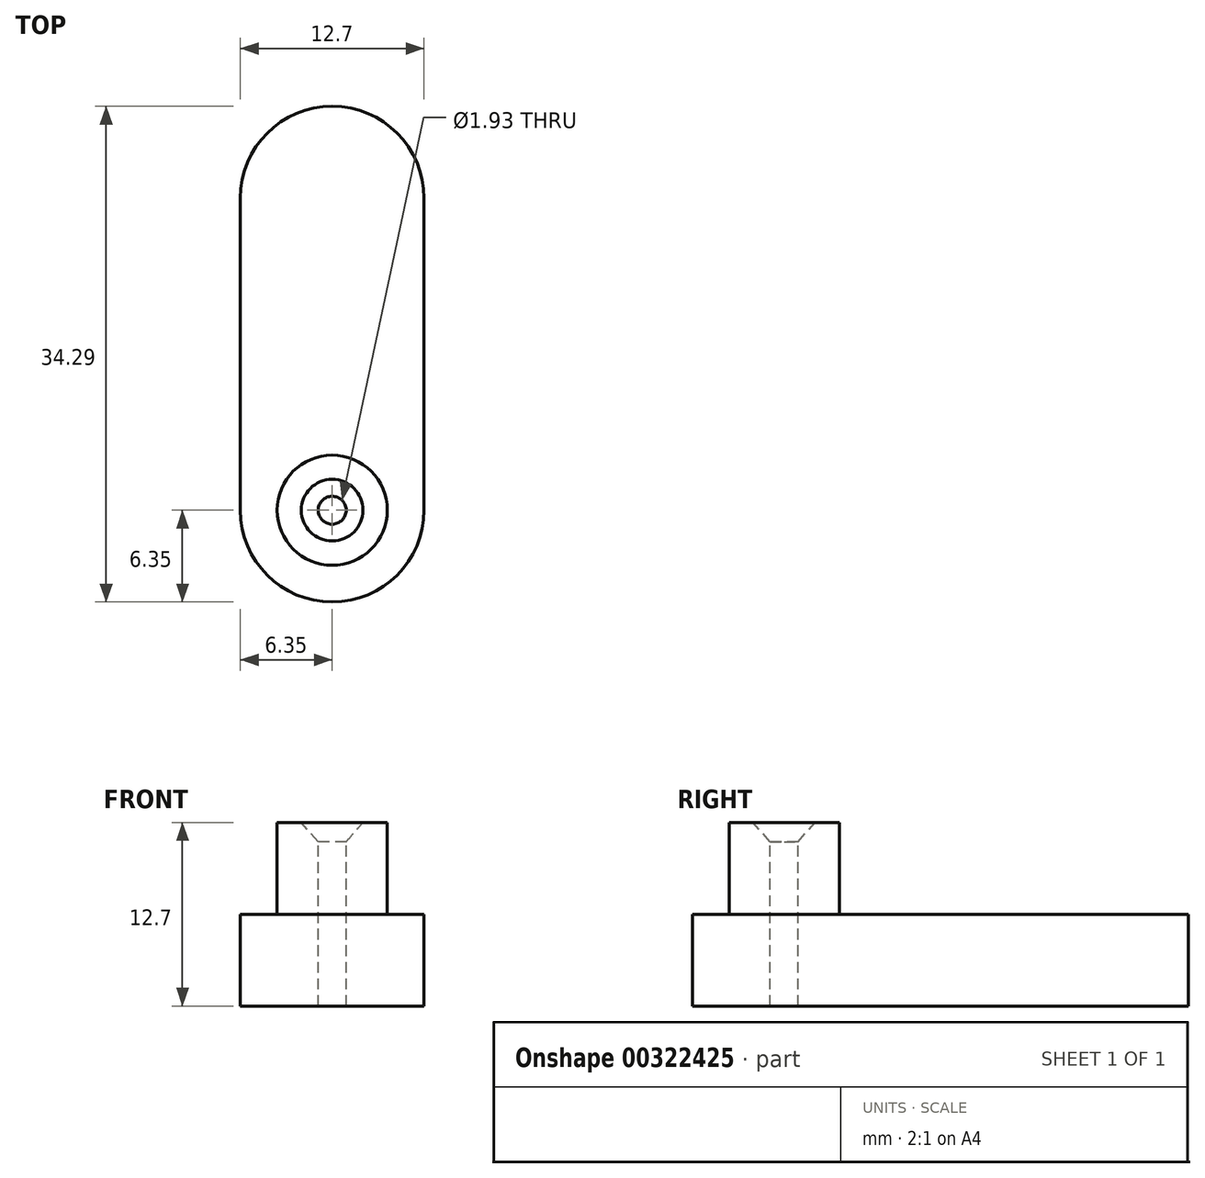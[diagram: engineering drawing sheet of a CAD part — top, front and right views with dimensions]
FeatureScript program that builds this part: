
annotation { "Feature Type Name" : "Feature", "Feature Type Description" : "" }
export const myFeature = defineFeature(function(context is Context, id is Id, definition is map)
    precondition{}
    {
        {
            var Q0;
            Q0=qCreatedBy(makeId("Top.planeOp"),FACE);
            var sketch = newSketch(context, id + "F0", { "sketchPlane" : qUnion([Q0])});
            skLineSegment(sketch, "E0", {"start": v(0, 12.7) * mm, "end": v(0, 34.3) * mm});
            skLineSegment(sketch, "E1", {"start": v(0, 34.3) * mm, "end": v(22.73, 67.98) * mm});
            skPoint(sketch, "E2", {"position": v(0, 0) * mm});
            skLineSegment(sketch, "E3", {"start": v(0, 12.7) * mm, "end": v(0, 0) * mm});
            skArc(sketch, "E4.0.startCap", {"start": v(6.35, 12.7) * mm, "mid": v(0, 6.35) * mm, "end": v(-6.35, 12.7) * mm});
            skArc(sketch, "E4.0.endCap", {"start": v(-6.35, 34.3) * mm, "mid": v(0, 40.64) * mm, "end": v(6.35, 34.3) * mm});
            skLineSegment(sketch, "E4.0.left", {"start": v(-6.35, 12.7) * mm, "end": v(-6.35, 34.3) * mm});
            skLineSegment(sketch, "E4.0.right", {"start": v(6.35, 12.7) * mm, "end": v(6.35, 34.3) * mm});
            skArc(sketch, "E4.1.startCap", {"start": v(-6.35, 12.7) * mm, "mid": v(0, 19.05) * mm, "end": v(6.35, 12.7) * mm});
            skArc(sketch, "E4.1.endCap", {"start": v(6.35, 0) * mm, "mid": v(0, -6.35) * mm, "end": v(-6.35, 0) * mm});
            skLineSegment(sketch, "E4.1.left", {"start": v(6.35, 12.7) * mm, "end": v(6.35, 0) * mm});
            skLineSegment(sketch, "E4.1.right", {"start": v(-6.35, 12.7) * mm, "end": v(-6.35, 0) * mm});
            skArc(sketch, "E4.2.startCap", {"start": v(5.26, 30.74) * mm, "mid": v(-3.55, 29.03) * mm, "end": v(-5.26, 37.84) * mm});
            skArc(sketch, "E4.2.endCap", {"start": v(17.46, 71.53) * mm, "mid": v(26.28, 73.25) * mm, "end": v(27.99, 64.43) * mm});
            skLineSegment(sketch, "E4.2.left", {"start": v(-5.26, 37.84) * mm, "end": v(17.46, 71.53) * mm});
            skLineSegment(sketch, "E4.2.right", {"start": v(5.26, 30.74) * mm, "end": v(27.99, 64.43) * mm});
            skSolve(sketch);
        }
        {
            var Q0;
            Q0=makeQuery(id+"F0.imprint","IMPRINT",FACE,{"disambiguationData":[TD([[makeQuery(id+"F0.imprint","IMPRINT",EDGE,{"derivedFrom":sQuery(id+"F0.wireOp",EDGE,"E4.1.endCap")}),-1.0]])]});
            var Q1;
            {var subQ0=sQuery(id+"F0.wireOp",EDGE,"E3");var subQ1=sQuery(id+"F0.wireOp",EDGE,"E0");var subQ2=makeQuery(id+"F0.imprint","INTERSECT",VERTEX,{"derivedFrom":[subQ1,subQ0]});Q1=makeQuery(id+"F0.imprint","IMPRINT",FACE,{"disambiguationData":[TD([[makeQuery(id+"F0.imprint","IMPRINT",EDGE,{"disambiguationData":[TD([[subQ2,-1.0]])],"derivedFrom":subQ1}),1.0]])]});}
            var Q2;
            {var subQ0=sQuery(id+"F0.wireOp",EDGE,"E3");var subQ1=sQuery(id+"F0.wireOp",EDGE,"E0");var subQ2=makeQuery(id+"F0.imprint","INTERSECT",VERTEX,{"derivedFrom":[subQ1,subQ0]});Q2=makeQuery(id+"F0.imprint","IMPRINT",FACE,{"disambiguationData":[TD([[makeQuery(id+"F0.imprint","IMPRINT",EDGE,{"disambiguationData":[TD([[subQ2,-1.0]])],"derivedFrom":subQ1}),-1.0]])]});}
            var Q3;
            {var subQ3=sQuery(id+"F0.wireOp",EDGE,"E0");var subQ5=sQuery(id+"F0.wireOp",EDGE,"E4.1.startCap");var subQ8=makeQuery(id+"F0.imprint","INTERSECT",VERTEX,{"derivedFrom":[subQ3,subQ5]});Q3=makeQuery(id+"F0.imprint","IMPRINT",FACE,{"disambiguationData":[TD([[makeQuery(id+"F0.imprint","IMPRINT",EDGE,{"disambiguationData":[TD([[subQ8,-1.0]])],"derivedFrom":subQ3}),-1.0]])]});}
            var Q4;
            {var subQ5=sQuery(id+"F0.wireOp",EDGE,"E4.0.left");Q4=makeQuery(id+"F0.imprint","IMPRINT",FACE,{"disambiguationData":[TD([[makeQuery(id+"F0.imprint","IMPRINT",EDGE,{"derivedFrom":subQ5}),-1.0]])]});}
            var Q5;
            {var subQ2=sQuery(id+"F0.wireOp",EDGE,"E0");var subQ6=sQuery(id+"F0.wireOp",EDGE,"E1");var subQ8=makeQuery(id+"F0.imprint","INTERSECT",VERTEX,{"derivedFrom":[subQ2,subQ6]});Q5=makeQuery(id+"F0.imprint","IMPRINT",FACE,{"disambiguationData":[TD([[makeQuery(id+"F0.imprint","IMPRINT",EDGE,{"disambiguationData":[TD([[subQ8,1.0]])],"derivedFrom":subQ2}),1.0]])]});}
            var Q6;
            {var subQ0=sQuery(id+"F0.wireOp",EDGE,"E4.2.endCap");Q6=makeQuery(id+"F0.imprint","IMPRINT",FACE,{"disambiguationData":[TD([[makeQuery(id+"F0.imprint","IMPRINT",EDGE,{"derivedFrom":subQ0}),-1.0]])]});}
            var Q7;
            {var subQ7=sQuery(id+"F0.wireOp",EDGE,"E1");var subQ9=sQuery(id+"F0.wireOp",EDGE,"E0");var subQ10=makeQuery(id+"F0.imprint","INTERSECT",VERTEX,{"derivedFrom":[subQ9,subQ7]});Q7=makeQuery(id+"F0.imprint","IMPRINT",FACE,{"disambiguationData":[TD([[makeQuery(id+"F0.imprint","IMPRINT",EDGE,{"disambiguationData":[TD([[subQ10,1.0]])],"derivedFrom":subQ9}),-1.0]])]});}
            var Q8;
            Q8 = qConstructionFilter(qBodyType(qCreatedBy(id + "F0" ,EDGE), BodyType.WIRE), ConstructionObject.NO);
            extrude(context, id + "F1", {"entities" : qUnion([Q0, Q1, Q2, Q3, Q4, Q5, Q6, Q7]), "surfaceEntities" : qUnion([Q8]), "depth" : 6.35 * mm});
        }
        {
            var Q0;
            Q0=makeQuery(id+"F1.opExtrude","CAP_FACE",FACE,{"disambiguationData":[OSD([sQuery(id+"F0.wireOp",EDGE,"E4.0.left"),sQuery(id+"F0.wireOp",EDGE,"E4.0.right"),sQuery(id+"F0.wireOp",EDGE,"E4.1.endCap"),sQuery(id+"F0.wireOp",EDGE,"E4.1.left"),sQuery(id+"F0.wireOp",EDGE,"E4.1.right"),sQuery(id+"F0.wireOp",EDGE,"E4.2.startCap"),sQuery(id+"F0.wireOp",EDGE,"E4.2.endCap"),sQuery(id+"F0.wireOp",EDGE,"E4.2.left"),sQuery(id+"F0.wireOp",EDGE,"E4.2.right")])],"isStart":false});
            var sketch = newSketch(context, id + "F2", { "sketchPlane" : qUnion([Q0])});
            skCircle(sketch, "E5", {"center": v(0, 12.7) * mm, "radius": 3.81 * mm});
            skSolve(sketch);
        }
        {
            var Q0;
            Q0 = qSketchRegion(id + "F2", true);
            extrude(context, id + "F3", {"entities" : qUnion([Q0]), "operationType" : NewBodyOperationType.ADD, "depth" : 6.35 * mm});
        }
        {
            var Q0;
            Q0=makeQuery(id+"F3.opExtrude","CAP_FACE",FACE,{"disambiguationData":[OSD([sQuery(id+"F2.wireOp",EDGE,"E5")])],"isStart":false});
            var sketch = newSketch(context, id + "F4", { "sketchPlane" : qUnion([Q0])});
            skPoint(sketch, "E6", {"position": v(0, 12.7) * mm});
            skSolve(sketch);
        }
        {
            var Q0;
            Q0=sQuery(id+"F4.wireOp",VERTEX,"E6");
            var Q1;
            Q1=makeQuery(id+"F1.opExtrude","SWEPT_BODY",BODY,{"disambiguationData":[OSD([sQuery(id+"F0.wireOp",EDGE,"E4.0.left"),sQuery(id+"F0.wireOp",EDGE,"E4.0.right"),sQuery(id+"F0.wireOp",EDGE,"E4.1.endCap"),sQuery(id+"F0.wireOp",EDGE,"E4.1.left"),sQuery(id+"F0.wireOp",EDGE,"E4.1.right"),sQuery(id+"F0.wireOp",EDGE,"E4.2.startCap"),sQuery(id+"F0.wireOp",EDGE,"E4.2.endCap"),sQuery(id+"F0.wireOp",EDGE,"E4.2.left"),sQuery(id+"F0.wireOp",EDGE,"E4.2.right")])]});
            hole(context, id + "F5", {"style" : HoleStyle.C_SINK, "endStyle" : HoleEndStyle.THROUGH, "standardTappedOrClearance" : lookupTablePath({ "standard" : "ANSI", "fit" : "Close", "size" : "#1", "type" : "Clearance" }), "standardBlindInLast" : lookupTablePath({ "fit" : "Close", "standard" : "ANSI", "size" : "#1", "type" : "Clearance" }), "holeDiameter" : 1.93 * mm, "cSinkDiameter" : 4.27 * mm, "cSinkAngle" : 82 * degree, "tappedDepth" : 12.7 * mm, "tapClearance" : 3, "locations" : qUnion([Q0]), "scope" : qUnion([Q1])});
        }
        {
            var Q0;
            Q0=sQuery(id+"F0.wireOp",VERTEX,"E2");
            var Q1;
            Q1=makeQuery(id+"F1.opExtrude","SWEPT_BODY",BODY,{"disambiguationData":[OSD([sQuery(id+"F0.wireOp",EDGE,"E4.0.left"),sQuery(id+"F0.wireOp",EDGE,"E4.0.right"),sQuery(id+"F0.wireOp",EDGE,"E4.1.endCap"),sQuery(id+"F0.wireOp",EDGE,"E4.1.left"),sQuery(id+"F0.wireOp",EDGE,"E4.1.right"),sQuery(id+"F0.wireOp",EDGE,"E4.2.startCap"),sQuery(id+"F0.wireOp",EDGE,"E4.2.endCap"),sQuery(id+"F0.wireOp",EDGE,"E4.2.left"),sQuery(id+"F0.wireOp",EDGE,"E4.2.right")])]});
            hole(context, id + "F6", {"style" : HoleStyle.SIMPLE, "endStyle" : HoleEndStyle.THROUGH, "oppositeDirection" : true, "holeDiameter" : 2.03 * mm, "tappedDepth" : 12.7 * mm, "tapClearance" : 3, "locations" : qUnion([Q0]), "scope" : qUnion([Q1])});
        }
    });
